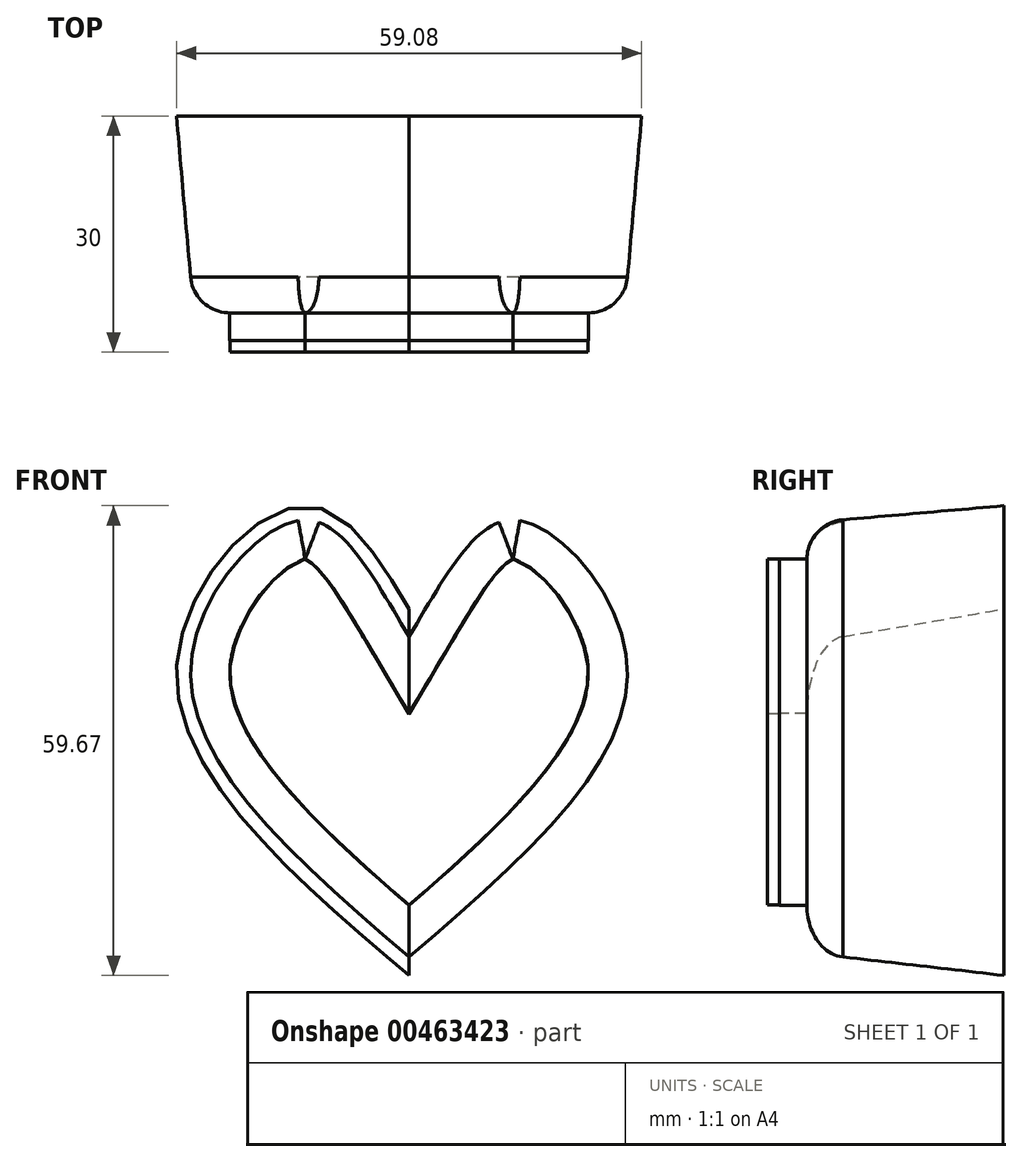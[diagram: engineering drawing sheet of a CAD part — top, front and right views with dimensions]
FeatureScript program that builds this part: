
annotation { "Feature Type Name" : "Feature", "Feature Type Description" : "" }
export const myFeature = defineFeature(function(context is Context, id is Id, definition is map)
    precondition{}
    {
        {
            var Q0;
            Q0=qCreatedBy(makeId("Front.planeOp"),FACE);
            var sketch = newSketch(context, id + "F0", { "sketchPlane" : qUnion([Q0])});
            skFitSpline(sketch, "E0", {"points": [v(0, -46.55) * mm, v(-29.52, -7.33) * mm, v(-13.62, 13.1) * mm, v(0, 0) * mm], "startDerivative": vector(-106.3, 90.46) * mm, "endDerivative": vector(45.36, -76.47) * mm});
            skFitSpline(sketch, "E1.MirrorCS", {"points": [v(0, -46.55) * mm, v(29.52, -7.33) * mm, v(13.62, 13.1) * mm, v(0, 0) * mm], "startDerivative": vector(106.3, 90.46) * mm, "endDerivative": vector(-45.36, -76.47) * mm});
            skSolve(sketch);
        }
        {
            var Q0;
            Q0=makeQuery(id+"F0.imprint","IMPRINT",FACE,{"disambiguationData":[TD([[makeQuery(id+"F0.imprint","IMPRINT",EDGE,{"derivedFrom":sQuery(id+"F0.wireOp",EDGE,"E0")}),-1.0]])]});
            extrude(context, id + "F1", {"entities" : qUnion([Q0]), "depth" : 25 * mm, "hasDraft" : true, "draftAngle" : 5 * degree, "draftPullDirection" : true});
        }
        {
            var Q0;
            Q0=makeQuery(id+"F1.opExtrude","CAP_EDGE",EDGE,{"disambiguationData":[OSD([sQuery(id+"F0.wireOp",EDGE,"E0")])],"isStart":false});
            var Q1;
            Q1=makeQuery(id+"F1.opExtrude","CAP_EDGE",EDGE,{"disambiguationData":[OSD([sQuery(id+"F0.wireOp",EDGE,"E1.MirrorCS")])],"isStart":false});
            fillet(context, id + "F2", {"entities" : qUnion([Q0, Q1]), "radius" : 5 * mm, "tangentPropagation" : true, "allowEdgeOverflow" : false});
        }
        {
            var Q0;
            Q0=qCreatedBy(makeId("Front.planeOp"),FACE);
            var sketch = newSketch(context, id + "F3", { "sketchPlane" : qUnion([Q0])});
            skText(sketch, "E2", { "text": "love you", "fontName": "OpenSans-Regular.ttf"});
            const initialGuessF3  = {"E2": [-0.02683, -0.01847, 1, 0, 0.0095]};
            skSetInitialGuess(sketch, initialGuessF3);
            skSolve(sketch);
        }
        {
            var Q0;
            Q0 = qSketchRegion(id + "F3", true);
            extrude(context, id + "F4", {"entities" : qUnion([Q0]), "operationType" : NewBodyOperationType.REMOVE, "oppositeDirection" : true, "depth" : 25 * mm});
        }
        {
            var Q0;
            Q0=qCreatedBy(makeId("Front.planeOp"),FACE);
            var sketch = newSketch(context, id + "F5", { "sketchPlane" : qUnion([Q0])});
            skText(sketch, "E3", { "text": "love u", "fontName": "OpenSans-Regular.ttf"});
            const initialGuessF5  = {"E3": [-0.013, -0.01992, 1, 0, 0.00681]};
            skSetInitialGuess(sketch, initialGuessF5);
            skSolve(sketch);
        }
        {
            var Q0;
            Q0 = qSketchRegion(id + "F5", true);
            extrude(context, id + "F6", {"entities" : qUnion([Q0]), "operationType" : NewBodyOperationType.REMOVE, "oppositeDirection" : true, "depth" : 5 * mm});
        }
        {
            var Q0;
            Q0=qCreatedBy(makeId("Front.planeOp"),FACE);
            var sketch = newSketch(context, id + "F7", { "sketchPlane" : qUnion([Q0])});
            skText(sketch, "E4", { "text": "love u", "fontName": "OpenSans-Regular.ttf"});
            const initialGuessF7  = {"E4": [-0.00888, -0.0222, 1, 0, 0.00578]};
            skSetInitialGuess(sketch, initialGuessF7);
            skSolve(sketch);
        }
        {
            var Q0;
            Q0 = qSketchRegion(id + "F7", true);
            extrude(context, id + "F8", {"entities" : qUnion([Q0]), "operationType" : NewBodyOperationType.REMOVE, "oppositeDirection" : true, "depth" : 7 * mm});
        }
        {
            var Q0;
            Q0=makeQuery(id+"F1.opExtrude","CAP_FACE",FACE,{"disambiguationData":[OSD([sQuery(id+"F0.wireOp",EDGE,"E0"),sQuery(id+"F0.wireOp",EDGE,"E1.MirrorCS")])],"isStart":false});
            extrude(context, id + "F9", {"entities" : qUnion([Q0]), "operationType" : NewBodyOperationType.ADD, "depth" : 3.5 * mm});
        }
        {
            var Q0;
            {var subQ0=sQuery(id+"F0.wireOp",EDGE,"E1.MirrorCS");var subQ1=sQuery(id+"F0.wireOp",EDGE,"E0");Q0=makeQuery(id+"F9.opExtrude","CAP_EDGE",EDGE,{"disambiguationData":[OSD([subQ1,subQ0]),TDD([makeQuery(id+"F2.opFillet","BLEND_EDGE",EDGE,{"blendedFrom":[makeQuery(id+"F1.opExtrude","CAP_EDGE",EDGE,{"disambiguationData":[OSD([subQ1])],"isStart":false}),makeQuery(id+"F1.opExtrude","CAP_FACE",FACE,{"disambiguationData":[OSD([subQ1,subQ0])],"isStart":false})],"blendedInto":[makeQuery(id+"F1.opExtrude","CAP_FACE",FACE,{"disambiguationData":[OSD([subQ1,subQ0])],"isStart":false})]})])],"isStart":false});}
            var Q1;
            {var subQ0=sQuery(id+"F0.wireOp",EDGE,"E1.MirrorCS");var subQ1=sQuery(id+"F0.wireOp",EDGE,"E0");Q1=makeQuery(id+"F9.opExtrude","CAP_EDGE",EDGE,{"disambiguationData":[OSD([subQ1,subQ0]),TDD([makeQuery(id+"F2.opFillet","BLEND_EDGE",EDGE,{"blendedFrom":[makeQuery(id+"F1.opExtrude","CAP_EDGE",EDGE,{"disambiguationData":[OSD([subQ0])],"isStart":false}),makeQuery(id+"F1.opExtrude","CAP_FACE",FACE,{"disambiguationData":[OSD([subQ1,subQ0])],"isStart":false})],"blendedInto":[makeQuery(id+"F1.opExtrude","CAP_FACE",FACE,{"disambiguationData":[OSD([subQ1,subQ0])],"isStart":false})]})])],"isStart":false});}
            fillet(context, id + "F10", {"entities" : qUnion([Q0, Q1]), "radius" : 0.02 * mm, "tangentPropagation" : true, "allowEdgeOverflow" : false});
        }
        {
            var Q0;
            Q0=makeQuery(id+"F9.opExtrude","CAP_FACE",FACE,{"disambiguationData":[OSD([sQuery(id+"F0.wireOp",EDGE,"E0"),sQuery(id+"F0.wireOp",EDGE,"E1.MirrorCS")])],"isStart":false});
            extrude(context, id + "F11", {"entities" : qUnion([Q0]), "operationType" : NewBodyOperationType.ADD, "depth" : 1.5 * mm});
        }
    });
